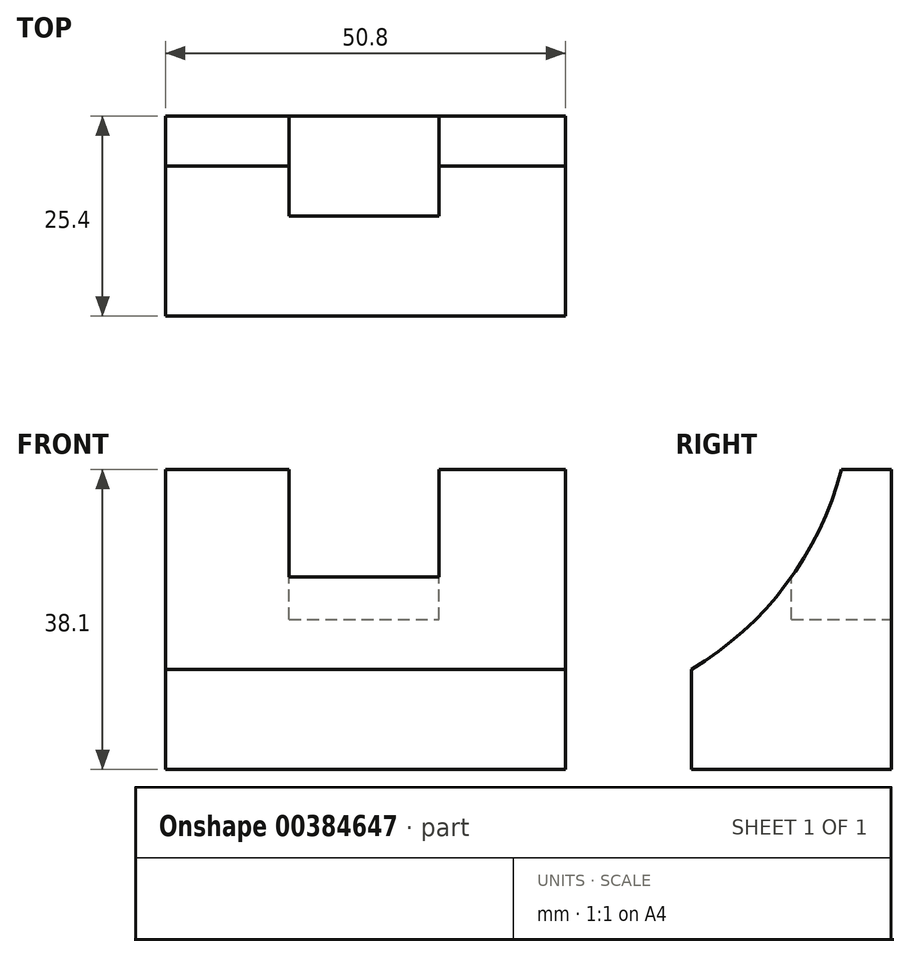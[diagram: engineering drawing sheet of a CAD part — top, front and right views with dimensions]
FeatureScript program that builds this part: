
annotation { "Feature Type Name" : "Feature", "Feature Type Description" : "" }
export const myFeature = defineFeature(function(context is Context, id is Id, definition is map)
    precondition{}
    {
        {
            var Q0;
            Q0=qCreatedBy(makeId("Front.planeOp"),FACE);
            var sketch = newSketch(context, id + "F0", { "sketchPlane" : qUnion([Q0])});
            skLineSegment(sketch, "E0", {"start": v(-8.52, 0) * mm, "end": v(-8.52, 38.1) * mm});
            skLineSegment(sketch, "E1", {"start": v(-8.52, 38.1) * mm, "end": v(42.28, 38.1) * mm});
            skLineSegment(sketch, "E2", {"start": v(42.28, 38.1) * mm, "end": v(42.28, 0) * mm});
            skLineSegment(sketch, "E3", {"start": v(42.28, 0) * mm, "end": v(-8.52, 0) * mm});
            skSolve(sketch);
        }
        {
            var Q0;
            Q0 = qSketchRegion(id + "F0", true);
            extrude(context, id + "F1", {"entities" : qUnion([Q0]), "depth" : 25.4 * mm});
        }
        {
            var Q0;
            Q0=makeQuery(id+"F1.opExtrude","SWEPT_FACE",FACE,{"disambiguationData":[OSD([sQuery(id+"F0.wireOp",EDGE,"E2")])]});
            var sketch = newSketch(context, id + "F2", { "sketchPlane" : qUnion([Q0])});
            skArc(sketch, "E4", {"start": v(-25.4, 12.7) * mm, "mid": v(-13.38, 23.53) * mm, "end": v(-6.35, 38.1) * mm});
            skLineSegment(sketch, "E5", {"start": v(-25.4, 12.7) * mm, "end": v(-25.4, 0) * mm});
            skLineSegment(sketch, "E6", {"start": v(-25.4, 0) * mm, "end": v(0, 0) * mm});
            skLineSegment(sketch, "E7", {"start": v(0, 0) * mm, "end": v(0, 38.1) * mm});
            skLineSegment(sketch, "E8", {"start": v(0, 38.1) * mm, "end": v(-6.35, 38.1) * mm});
            skSolve(sketch);
        }
        {
            var Q0;
            {var subQ0=sQuery(id+"F2.wireOp",EDGE,"E4");Q0=makeQuery(id+"F2.imprint","IMPRINT",FACE,{"disambiguationData":[TD([[makeQuery(id+"F2.imprint","IMPRINT",EDGE,{"derivedFrom":subQ0}),1.0]])]});}
            extrude(context, id + "F3", {"entities" : qUnion([Q0]), "operationType" : NewBodyOperationType.REMOVE, "oppositeDirection" : true, "depth" : 50.8 * mm});
        }
        {
            var Q0;
            Q0=makeQuery(id+"F1.opExtrude","SWEPT_FACE",FACE,{"disambiguationData":[OSD([sQuery(id+"F0.wireOp",EDGE,"E1")])]});
            var sketch = newSketch(context, id + "F4", { "sketchPlane" : qUnion([Q0])});
            skLineSegment(sketch, "E9", {"start": v(7.18, 0) * mm, "end": v(7.18, -12.7) * mm});
            skLineSegment(sketch, "E10", {"start": v(7.18, -12.7) * mm, "end": v(26.23, -12.7) * mm});
            skLineSegment(sketch, "E11", {"start": v(26.23, -12.7) * mm, "end": v(26.23, 0) * mm});
            skLineSegment(sketch, "E12", {"start": v(26.23, 0) * mm, "end": v(7.18, 0) * mm});
            skSolve(sketch);
        }
        {
            var Q0;
            Q0 = qSketchRegion(id + "F4", true);
            extrude(context, id + "F5", {"entities" : qUnion([Q0]), "operationType" : NewBodyOperationType.REMOVE, "oppositeDirection" : true, "depth" : 19.05 * mm});
        }
    });
